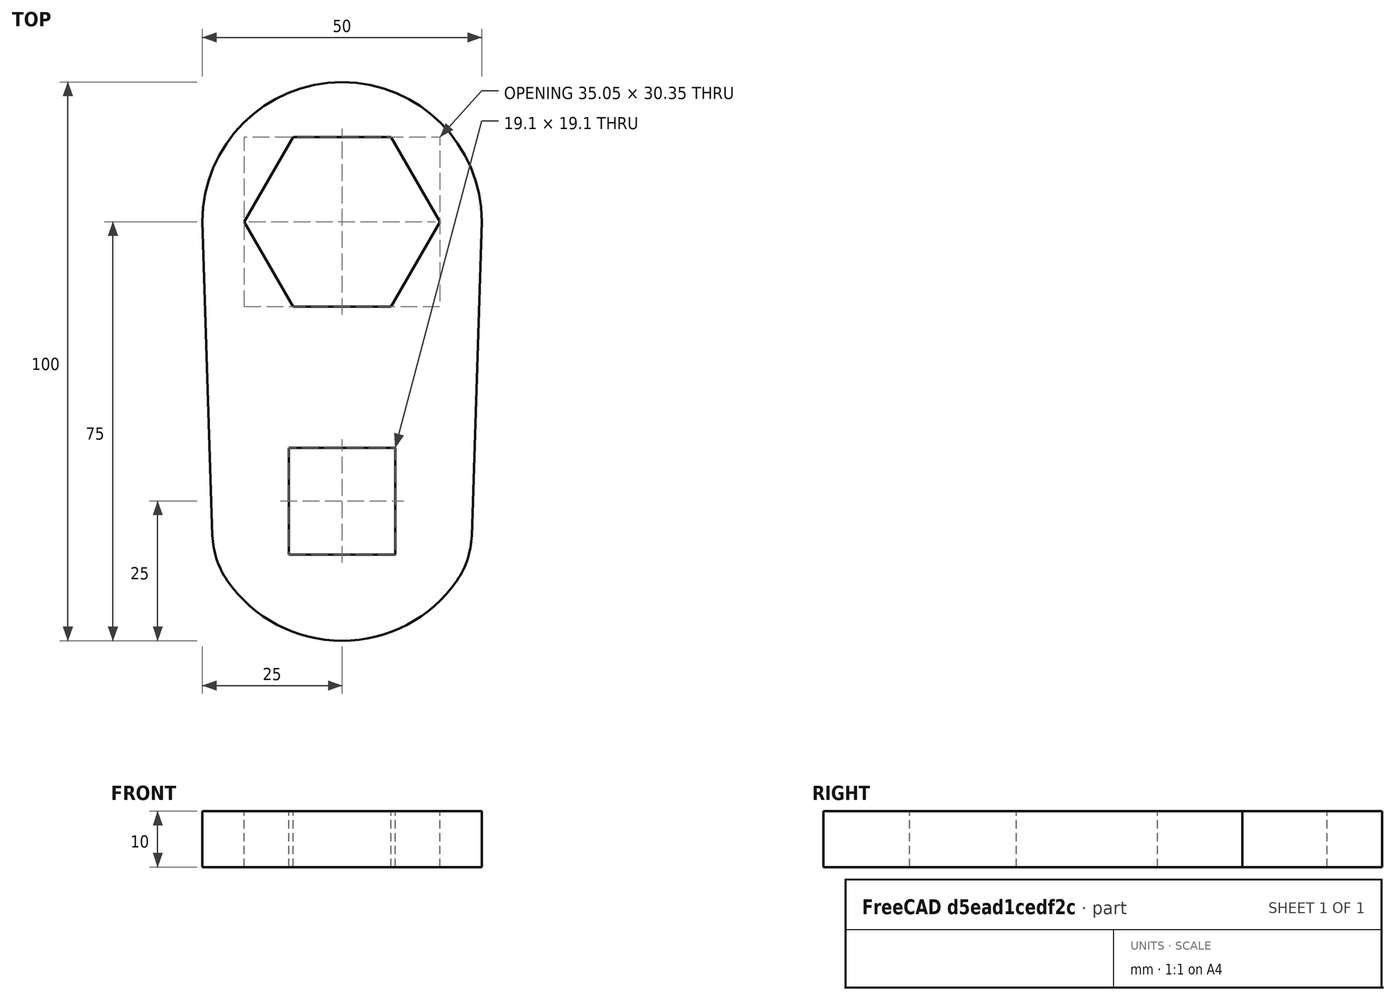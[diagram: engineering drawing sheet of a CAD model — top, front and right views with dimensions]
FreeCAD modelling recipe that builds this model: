
FCSTD DOCUMENT  (FreeCAD 0.18R16131 (Git))
Label: transmission wrench 35 19 w fea
License: All rights reserved
LicenseURL: http://en.wikipedia.org/wiki/All_rights_reserved
objects: Fem::FemMeshObjectPython×2, Sketcher::SketchObject×1, PartDesign::Pad×1, PartDesign::Fillet×1, PartDesign::Body×1, Fem::FemSolverObjectPython×1, Fem::ConstraintFixed×1, Fem::ConstraintForce×1, App::MaterialObjectPython×1, Fem::FemResultObjectPython×1, Fem::FemAnalysis×1
note: 5 computed .brp shape members not serialized (recipe doc carries the construction recipe); baked Part::Feature solids carry a one-line shape summary decoded from their .brp

FEATURE [Sketcher::SketchObject] Sketch
  MapMode = 5
  Support = -> [XY_Plane]
  expr: Constraints[29] = 25.4 * 0.75 + 0.05
  sketch-geometry (17):
    g0: LineSegment StartX=-17.525 StartY=0 StartZ=0 EndX=-8.7625 EndY=-15.1771 EndZ=0
    g1: LineSegment StartX=-8.7625 StartY=-15.1771 StartZ=0 EndX=8.7625 EndY=-15.1771 EndZ=0
    g2: LineSegment StartX=8.7625 StartY=-15.1771 StartZ=0 EndX=17.525 EndY=0 EndZ=0
    g3: LineSegment StartX=17.525 StartY=0 StartZ=0 EndX=8.7625 EndY=15.1771 EndZ=0
    g4: LineSegment StartX=8.7625 StartY=15.1771 StartZ=0 EndX=-8.7625 EndY=15.1771 EndZ=0
    g5: LineSegment StartX=-8.7625 StartY=15.1771 StartZ=0 EndX=-17.525 EndY=0 EndZ=0
    g6: Circle [constr] CenterX=0 CenterY=0 CenterZ=0 NormalX=0 NormalY=0 NormalZ=1 AngleXU=0 Radius=17.525
    g7: LineSegment StartX=9.55 StartY=-59.55 StartZ=0 EndX=9.55 EndY=-40.45 EndZ=0
    g8: LineSegment StartX=9.55 StartY=-40.45 StartZ=0 EndX=-9.55 EndY=-40.45 EndZ=0
    g9: LineSegment StartX=-9.55 StartY=-40.45 StartZ=0 EndX=-9.55 EndY=-59.55 EndZ=0
    g10: LineSegment StartX=-9.55 StartY=-59.55 StartZ=0 EndX=9.55 EndY=-59.55 EndZ=0
    g11: Circle [constr] CenterX=0 CenterY=-50 CenterZ=0 NormalX=0 NormalY=0 NormalZ=1 AngleXU=0 Radius=13.5057
    g12: ArcOfCircle CenterX=0 CenterY=0 CenterZ=0 NormalX=0 NormalY=0 NormalZ=1 AngleXU=0 Radius=25 StartAngle=0 EndAngle=3.14159
    g13: ArcOfCircle CenterX=0 CenterY=-50 CenterZ=0 NormalX=0 NormalY=0 NormalZ=1 AngleXU=0 Radius=25 StartAngle=3.53355 EndAngle=5.89123
    g14: LineSegment StartX=-25 StartY=0 StartZ=0 EndX=-23.1041 EndY=-59.55 EndZ=0
    g15: LineSegment StartX=23.1041 StartY=-59.55 StartZ=0 EndX=25 EndY=0 EndZ=0
    g16: LineSegment [constr] StartX=-23.1041 StartY=-59.55 StartZ=0 EndX=23.1041 EndY=-59.55 EndZ=0
  constraints (44):
    c: Coincident(g0,g1)
    c: Coincident(g1,g2)
    c: Coincident(g2,g3)
    c: Coincident(g3,g4)
    c: Coincident(g4,g5)
    c: Coincident(g5,g0)
    c: Equal(g0, g1-g5) x5
    c: PointOnObject(g0,g6)
    c: PointOnObject(g1,g6)
    c: PointOnObject(g2,g6)
    c: PointOnObject(g3,g6)
    c: Symmetric(g0,g2,g-1)
    c: Coincident(g7,g8)
    c: Coincident(g8,g9)
    c: Coincident(g9,g10)
    c: Coincident(g10,g7)
    c: Equal(g7,g8)
    c: Equal(g7,g9)
    c: Equal(g7,g10)
    c: PointOnObject(g7,g11)
    c: PointOnObject(g8,g11)
    c: PointOnObject(g9,g11)
    c: PointOnObject(g10,g11)
    c: PointOnObject(g11,g-2)
    c: Parallel(g8,g-1)
    c: DistanceX(g9,g7) = 19.1
    c: DistanceY(g11,g-1) = 50
    c: PointOnObject(g12,g-1)
    c: PointOnObject(g12,g-1)
    c: Coincident(g14,g12)
    c: Coincident(g15,g12)
    c: Coincident(g12,g-1)
    c: Radius(g12) = 25
    c: Radius(g13) = 25
    c: Coincident(g15,g13)
    c: Coincident(g13,g14)
    c: Coincident(g13,g11)
    c: Coincident(g13,g16)
    c: Coincident(g16,g13)
    c: Parallel(g16,g-1)
    c: PointOnObject(g7,g16)
    c: Coincident(g6,g12)
    c: PointOnObject(g0,g-1)
    c: DistanceX(g0,g2) = 35.05
FEATURE [PartDesign::Pad] Pad
  Length = 10
  Length2 = 100
  Profile = -> Sketch
  Type = 0
FEATURE [PartDesign::Fillet] Fillet
  Base = -> Pad [Edge2,Edge5,Edge8,Edge1]
  BaseFeature = -> Pad
  Radius = 15
FEATURE [PartDesign::Body] Body
  Group = -> [Sketch,Pad,Fillet]
  Origin = -> Origin
  Tip = -> Fillet
FEATURE [Fem::FemSolverObjectPython] CalculiXccxTools  # FEM object (typed FeaturePython)
  AnalysisType = 0
  BeamShellResultOutput3D = false
  EigenmodeHighLimit = 1000000
  EigenmodeLowLimit = 0
  EigenmodesCount = 10
  GeometricalNonlinearity = 0
  IterationsControlParameterCutb = 0.25,0.5,0.75,0.85,,,1.5,
  IterationsControlParameterIter = 4,8,9,200,10,400,,200,,
  IterationsControlParameterTimeUse = false
  IterationsThermoMechMaximum = 200
  IterationsUserDefinedIncrementations = false
  IterationsUserDefinedTimeStepLength = false
  MaterialNonlinearity = 0
  MatrixSolverType = 0
  SplitInputWriter = false
  ThermoMechSteadyState = true
  TimeEnd = 1
  TimeInitialStep = 1
FEATURE [Fem::FemMeshObjectPython] FEMMeshGmsh  # FEM object (typed FeaturePython)
  Algorithm2D = 0
  Algorithm3D = 0
  CharacteristicLengthMax = 0
  CharacteristicLengthMin = 0
  CoherenceMesh = true
  ElementDimension = 0
  ElementOrder = 1
  GeometryTolerance = 1e-06
  GroupsOfNodes = false
  HighOrderOptimize = false
  OptimizeNetgen = false
  OptimizeStd = true
  Part = -> Fillet
  RecombineAll = false
FEATURE [Fem::ConstraintFixed] FemConstraintFixed
  NormalDirection = (0.866025,0.5,0)
  Normals = (54) [(0.866025,0.5,0),(0.866025,0.5,0),(0.866025,0.5,0),(0.866025,0.5,0),(0.866025,0.5,0),(0.866025,0.5,0),(0.866025,0.5,0),(0.866025,0.5,0),+46 more]
  Points = (54) [(-17.525,0,10),(-13.1437,-7.58855,10),(-8.7625,-15.1771,10),(-17.525,0,5),(-13.1437,-7.58855,5),(-8.7625,-15.1771,5),(-17.525,0,0),+47 more]
  References = -> [Fillet]
FEATURE [Fem::ConstraintForce] FemConstraintForce
  DirectionVector = (-1,3e-16,0)
  Force = 8300
  NormalDirection = (1,-3e-16,0)
  Points = (9) [(-9.55,-40.45,10),(-9.55,-50,10),(-9.55,-59.55,10),(-9.55,-40.45,5),(-9.55,-50,5),(-9.55,-59.55,5),(-9.55,-40.45,0),(-9.55,-50,0),(-9.55,-59.55,0)]
  References = -> [Fillet]
  Reversed = true
FEATURE [App::MaterialObjectPython] SolidMaterial  # material (typed FeaturePython)
  Category = 0
  Material = Density=7900 kg/m^3,Description=Standard steel material for CalculiX sample calculations,Father=Metal,Name=CalculiX-Steel,PoissonRatio=0.3,+4 more (map truncated)
FEATURE [Fem::FemMeshObjectPython] Result_mesh  # FEM object (typed FeaturePython)
FEATURE [Fem::FemResultObjectPython] CalculiX_static_results  # FEM object (typed FeaturePython)
  DisplacementLengths = [0.040063,0.00159334,0.0400837,0.00162549,0.0432859,0.00142389,0.0406304,0.0339214,0,0,0,0,0,0,0.0407583,0.0361397,0.0171075,0.0136078,0.0433307,0.00144617,0.0406614,0.0339355,0,0,0,0,0,0,0.0407367,0.0362702,0.0173906,0.0135766,0.00412428,+1024 more]
  DisplacementVectors = (1057) [(-0.0380997,0.0123862,0.000194739),(-0.000177722,0.00157163,-0.000192679),(-0.0381485,0.0122908,-0.000572281),(-0.000160981,0.00160638,0.000189322),+1053 more]
  Eigenmode = 0
  EigenmodeFrequency = 0
  MaxShear = [29.1858,17.3412,29.4979,14.1901,22.1065,15.5496,12.908,3.13337,2.94355,21.2501,2.47426,18.8036,37.5922,36.2756,32.2859,38.8916,61.2338,38.3822,22.395,12.7372,12.456,2.94777,2.7506,19.9406,2.67913,17.6184,37.3946,37.5265,29.7351,42.1386,+1027 more]
  Mesh = -> Result_mesh
  NodeNumbers = [1,2,3,4,5,6,7,8,9,10,11,12,13,14,15,16,17,18,19,20,21,22,23,24,25,26,27,28,29,30,31,32,33,34,35,36,37,38,39,40,41,42,43,44,45,46,47,48,49,50,51,52,53,54,55,56,57,58,59,60,61,62,63,64,65,66,67,68,69,+988 more]
  PrincipalMax = [57.5443,2.00636,57.7701,1.47842,43.246,29.3367,0.405533,0.706902,2.28351,11.9483,2.87603,27.012,47.5242,34.6152,-1.23509,90.8643,136.614,-7.98843,44.1368,24.2129,0.135733,0.646525,2.33747,14.1705,3.22416,22.4667,48.2559,24.8118,2.23106,+1028 more]
  PrincipalMed = [0.84094,-0.996337,0.279984,0.502919,0.619067,0.895554,-0.0608272,-0.627106,-0.280171,-3.47194,0.11716,3.11602,3.91476,0.171297,-9.30778,28.8259,22.9813,-22.9678,0.191182,-0.387016,-1.15744,-0.81839,-0.104013,-1.27094,0.212967,1.04543,+1031 more]
  PrincipalMin = [-0.827271,-32.676,-1.22556,-26.9017,-0.96693,-1.76251,-25.4104,-5.55984,-3.6036,-30.5518,-2.0725,-10.5952,-27.6603,-37.9361,-65.807,13.081,14.146,-84.7528,-0.653262,-1.26143,-24.7762,-5.24901,-3.16372,-25.7107,-2.1341,-12.77,-26.5333,+1030 more]
  ResultType = Fem::FemResultMechanical
  Stats = [-0.0444566,-0.0165214,0.000204923,-0.013013,0.000382466,0.014809,-0.000999247,-4.5744e-05,0.000984624,0,0.0173691,0.0444747,0.157566,37.236,132.186,-18.4248,21.4396,153.869,-60.7478,-0.505757,37.9888,-102.997,-18.9932,20.6367,0.0870032,+14 more]
  StrainVectors = (1057) [(-7.98221e-05,0.000266946,-7.74894e-05),(5.65251e-05,-0.00015676,3.99188e-05),(-8.27045e-05,0.000270344,-7.94021e-05),+1054 more]
  StressValues = [57.5556,33.2827,58.2575,27.9052,43.4417,29.8591,25.5859,5.71766,5.11252,37.265,4.29499,32.9645,65.3891,62.8579,60.9379,71.2281,118.298,70.4788,44.3739,25.0486,24.2912,5.31666,4.77419,34.83,4.65226,30.7519,64.9364,65.3659,55.6672,77.0585,+1027 more]
  StressVectors = (1057) [(0.388261,56.4046,0.765078),(1.82346,-32.6303,-0.859102),(-0.246605,56.7843,0.286867),(1.04011,-26.4565,0.495993),(12.2253,30.0398,0.633085),+1052 more]
  Time = 0
FEATURE [Fem::FemAnalysis] Analysis
  Group = -> [CalculiXccxTools,FEMMeshGmsh,FemConstraintFixed,FemConstraintForce,SolidMaterial,CalculiX_static_results]
